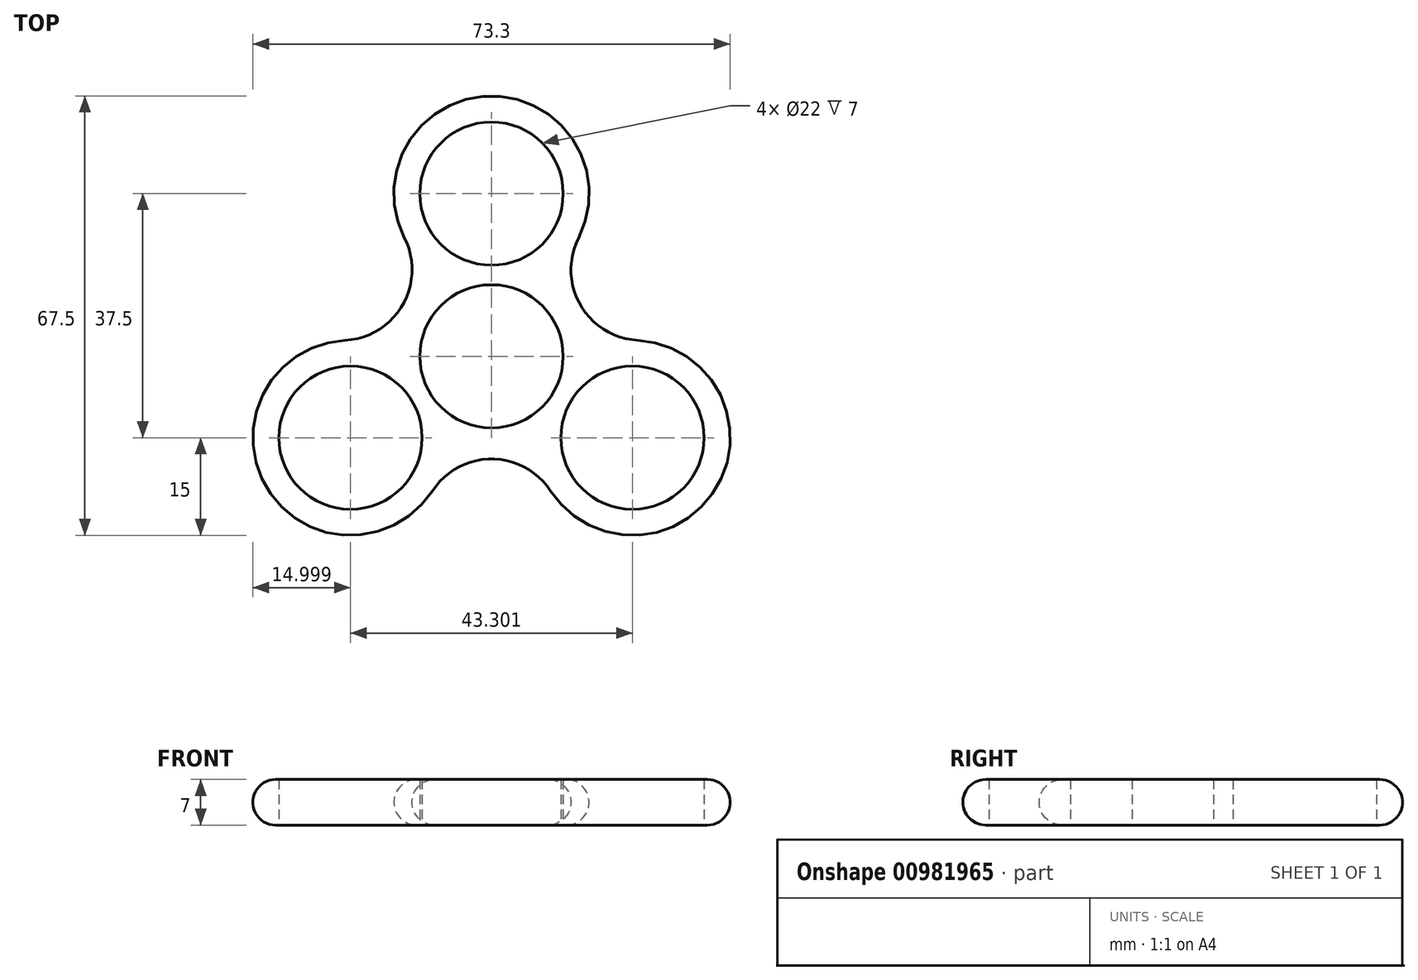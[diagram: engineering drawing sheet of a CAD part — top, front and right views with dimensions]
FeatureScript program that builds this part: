
annotation { "Feature Type Name" : "Feature", "Feature Type Description" : "" }
export const myFeature = defineFeature(function(context is Context, id is Id, definition is map)
    precondition{}
    {
        {
            var Q0;
            Q0=qCreatedBy(makeId("Top.planeOp"),FACE);
            var sketch = newSketch(context, id + "F0", { "sketchPlane" : qUnion([Q0])});
            skCircle(sketch, "E0", {"center": v(0, 0) * mm, "radius": 11 * mm});
            skCircle(sketch, "E1", {"center": v(0, 25) * mm, "radius": 11 * mm});
            skArc(sketch, "E2", {"start": v(13.37, 18.2) * mm, "mid": v(0, 40) * mm, "end": v(-13.37, 18.2) * mm});
            skArc(sketch, "E3.1.0", {"start": v(-22.46, 2.48) * mm, "mid": v(-34.64, -20) * mm, "end": v(-9.08, -20.69) * mm});
            skCircle(sketch, "E3.1.1", {"center": v(-21.65, -12.5) * mm, "radius": 11 * mm});
            skArc(sketch, "E3.2.0", {"start": v(9.08, -20.69) * mm, "mid": v(34.64, -20) * mm, "end": v(22.46, 2.48) * mm});
            skCircle(sketch, "E3.2.1", {"center": v(21.65, -12.5) * mm, "radius": 11 * mm});
            skArc(sketch, "E4", {"start": v(-24.92, 2.63) * mm, "mid": v(-24.9, 2.62) * mm, "end": v(-24.86, 2.62) * mm});
            skArc(sketch, "E5.1.0", {"start": v(9.08, -20.69) * mm, "mid": v(0, -15.76) * mm, "end": v(-9.08, -20.69) * mm});
            skArc(sketch, "E5.2.0", {"start": v(13.37, 18.2) * mm, "mid": v(13.65, 7.88) * mm, "end": v(22.46, 2.48) * mm});
            skArc(sketch, "E6.trimOffspring", {"start": v(24.86, 2.62) * mm, "mid": v(24.9, 2.62) * mm, "end": v(24.92, 2.63) * mm});
            skArc(sketch, "E7.trimOffspring", {"start": v(-22.46, 2.48) * mm, "mid": v(-13.65, 7.88) * mm, "end": v(-13.37, 18.2) * mm});
            skSolve(sketch);
        }
        {
            var Q0;
            Q0=makeQuery(id+"F0.imprint","IMPRINT",FACE,{"disambiguationData":[TD([[makeQuery(id+"F0.imprint","IMPRINT",EDGE,{"derivedFrom":sQuery(id+"F0.wireOp",EDGE,"E0")}),-1.0]])]});
            extrude(context, id + "F1", {"entities" : qUnion([Q0]), "depth" : 7 * mm, "offsetDistance" : 25 * mm});
        }
        {
            var Q0;
            Q0=makeQuery(id+"F1.opExtrude","CAP_EDGE",EDGE,{"disambiguationData":[OSD([sQuery(id+"F0.wireOp",EDGE,"E3.1.0")])],"isStart":false});
            fillet(context, id + "F2", {"entities" : qUnion([Q0]), "radius" : (7 / 2) * mm, "tangentPropagation" : true, "allowEdgeOverflow" : false});
        }
        {
            var Q0;
            Q0=makeQuery(id+"F1.opExtrude","CAP_EDGE",EDGE,{"disambiguationData":[OSD([sQuery(id+"F0.wireOp",EDGE,"E7.trimOffspring")])],"isStart":true});
            fillet(context, id + "F3", {"entities" : qUnion([Q0]), "radius" : (7 / 2) * mm, "tangentPropagation" : true, "allowEdgeOverflow" : false});
        }
    });
